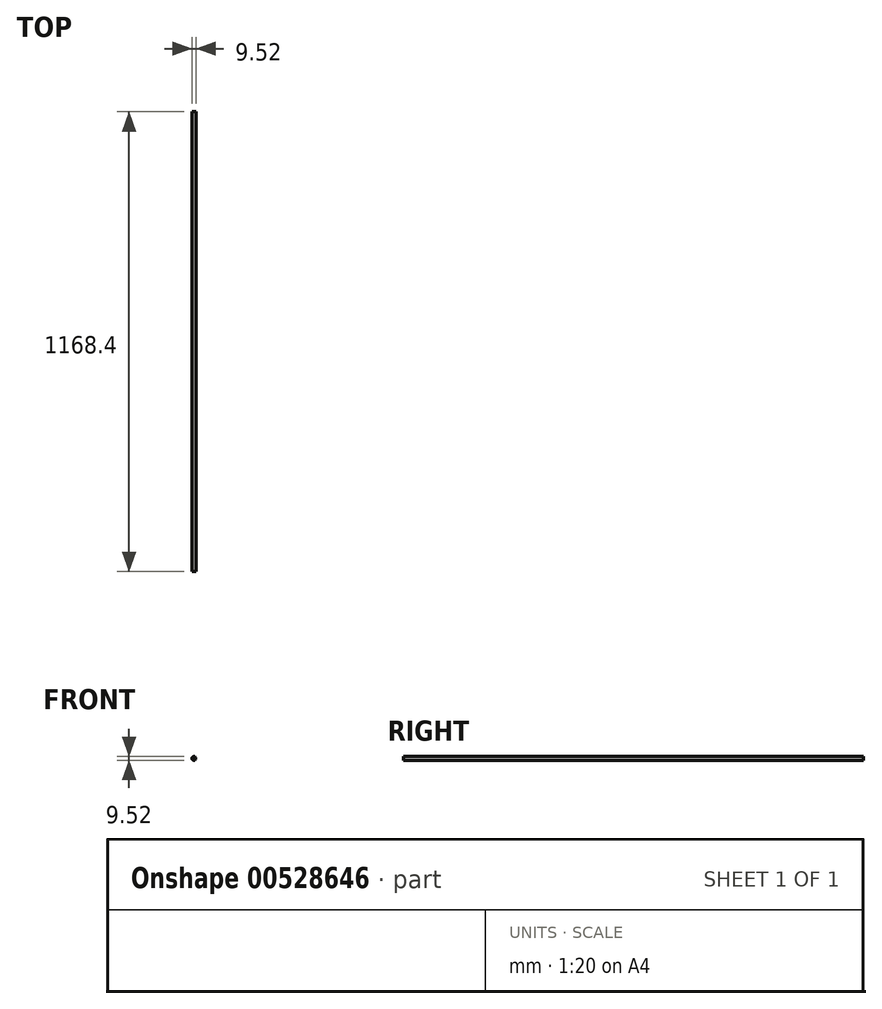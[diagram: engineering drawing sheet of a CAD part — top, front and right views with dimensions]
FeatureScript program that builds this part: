
annotation { "Feature Type Name" : "Feature", "Feature Type Description" : "" }
export const myFeature = defineFeature(function(context is Context, id is Id, definition is map)
    precondition{}
    {
        {
            var Q0;
            Q0=qCreatedBy(makeId("Front.planeOp"),FACE);
            var sketch = newSketch(context, id + "F0", { "sketchPlane" : qUnion([Q0])});
            skCircle(sketch, "E0", {"center": v(0, 0) * mm, "radius": 4.76 * mm});
            skSolve(sketch);
        }
        {
            var Q0;
            Q0=makeQuery(id+"F0.imprint","IMPRINT",FACE,{"disambiguationData":[TD([[makeQuery(id+"F0.imprint","IMPRINT",EDGE,{"derivedFrom":sQuery(id+"F0.wireOp",EDGE,"E0")}),1.0]])]});
            extrude(context, id + "F1", {"entities" : qUnion([Q0]), "depth" : 1168.4 * mm, "offsetDistance" : 25.4 * mm});
        }
    });
